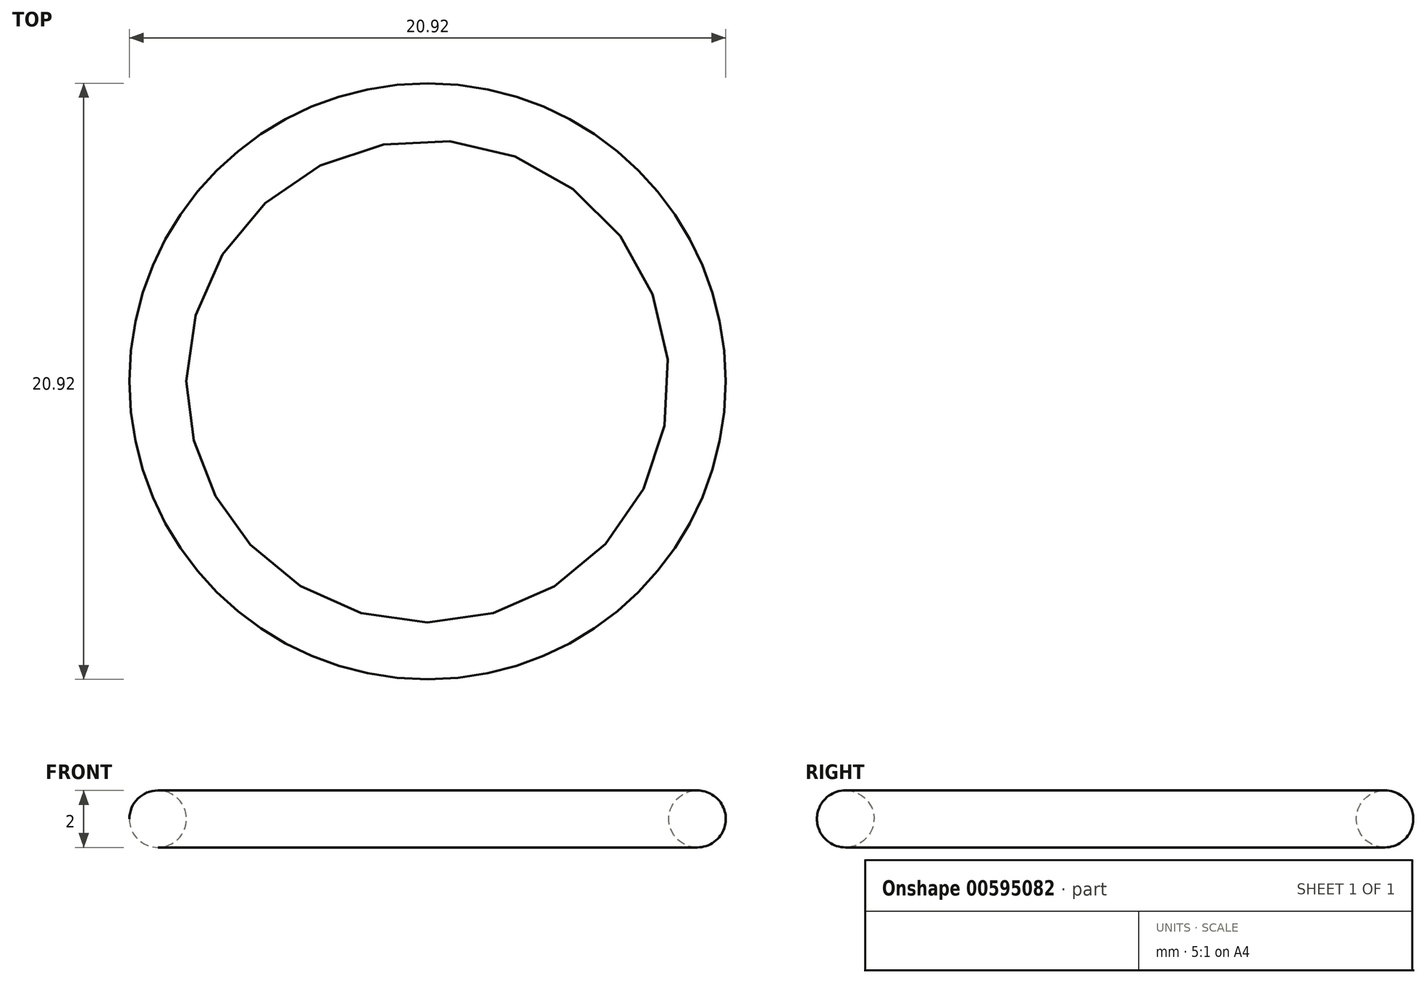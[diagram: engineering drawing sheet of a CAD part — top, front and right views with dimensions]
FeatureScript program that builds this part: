
annotation { "Feature Type Name" : "Feature", "Feature Type Description" : "" }
export const myFeature = defineFeature(function(context is Context, id is Id, definition is map)
    precondition{}
    {
        {
            var Q0;
            Q0=qCreatedBy(makeId("Front.planeOp"),FACE);
            var sketch = newSketch(context, id + "F0", { "sketchPlane" : qUnion([Q0])});
            skCircle(sketch, "E0", {"center": v(9.46, 0) * mm, "radius": 1 * mm});
            skLineSegment(sketch, "E1", {"start": v(0, 0) * mm, "end": v(0, 9.06) * mm, "construction": true});
            skSolve(sketch);
        }
        {
            var Q0;
            Q0=makeQuery(id+"F0.imprint","IMPRINT",FACE,{"disambiguationData":[TD([[makeQuery(id+"F0.imprint","IMPRINT",EDGE,{"derivedFrom":sQuery(id+"F0.wireOp",EDGE,"E0")}),1.0]])]});
            var Q1;
            Q1=sQuery(id+"F0.wireOp",EDGE,"E1");
            revolve(context, id + "F1", {"entities" : qUnion([Q0]), "axis" : qUnion([Q1]), "revolveType" : RevolveType.FULL});
        }
    });
